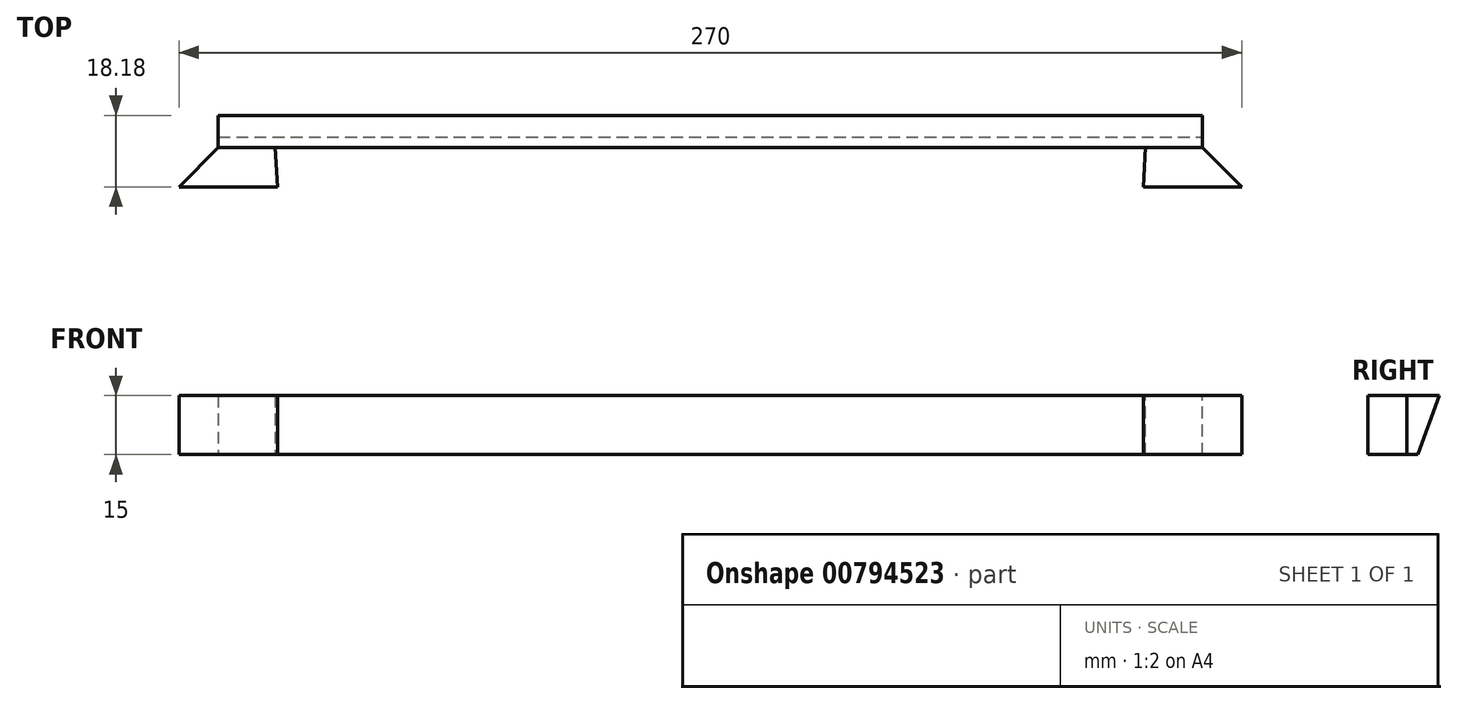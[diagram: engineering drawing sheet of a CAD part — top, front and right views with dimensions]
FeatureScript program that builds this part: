
annotation { "Feature Type Name" : "Feature", "Feature Type Description" : "" }
export const myFeature = defineFeature(function(context is Context, id is Id, definition is map)
    precondition{}
    {
        {
            var Q0;
            Q0=qCreatedBy(makeId("Front.planeOp"),FACE);
            var sketch = newSketch(context, id + "F0", { "sketchPlane" : qUnion([Q0])});
            skLineSegment(sketch, "E0.bottom", {"start": v(135, 7.5) * mm, "end": v(-135, 7.5) * mm});
            skLineSegment(sketch, "E0.top", {"start": v(135, -7.5) * mm, "end": v(-135, -7.5) * mm});
            skLineSegment(sketch, "E0.left", {"start": v(135, 7.5) * mm, "end": v(135, -7.5) * mm});
            skLineSegment(sketch, "E0.right", {"start": v(-135, 7.5) * mm, "end": v(-135, -7.5) * mm});
            skPoint(sketch, "E0.middle", {"position": v(0, 0) * mm});
            skSolve(sketch);
        }
        {
            var Q0;
            Q0 = qSketchRegion(id + "F0", true);
            extrude(context, id + "F1", {"entities" : qUnion([Q0]), "depth" : 10 * mm, "offsetDistance" : 25 * mm});
        }
        {
            var Q0;
            Q0=makeQuery(id+"F1.opExtrude","CAP_EDGE",EDGE,{"disambiguationData":[OSD([sQuery(id+"F0.wireOp",EDGE,"E0.left")])],"isStart":true});
            var Q1;
            Q1=makeQuery(id+"F1.opExtrude","CAP_EDGE",EDGE,{"disambiguationData":[OSD([sQuery(id+"F0.wireOp",EDGE,"E0.right")])],"isStart":true});
            chamfer(context, id + "F2", {"entities" : qUnion([Q0, Q1]), "width" : 10 * mm, "tangentPropagation" : true});
        }
        {
            var Q0;
            Q0=makeQuery(id+"F1.opExtrude","CAP_FACE",FACE,{"disambiguationData":[OSD([sQuery(id+"F0.wireOp",EDGE,"E0.bottom"),sQuery(id+"F0.wireOp",EDGE,"E0.top"),sQuery(id+"F0.wireOp",EDGE,"E0.left"),sQuery(id+"F0.wireOp",EDGE,"E0.right")])],"isStart":true});
            var sketch = newSketch(context, id + "F3", { "sketchPlane" : qUnion([Q0])});
            skSolve(sketch);
        }
        {
            var Q0;
            Q0 = qSketchRegion(id + "F3", true);
            var Q1;
            {var subQ0=sQuery(id+"F0.wireOp",EDGE,"E0.bottom");Q1=makeQuery(id+"F3.imprint","IMPRINT",FACE,{"disambiguationData":[TD([[makeQuery(id+"F3.imprint","IMPRINT",EDGE,{"derivedFrom":makeQuery(id+"F1.opExtrude","CAP_EDGE",EDGE,{"disambiguationData":[OSD([subQ0])],"isStart":true})}),-1.0]])]});}
            extrude(context, id + "F4", {"entities" : qUnion([Q0, Q1]), "depth" : 10 * mm, "offsetDistance" : 25 * mm});
        }
        {
            var Q0;
            Q0=makeQuery(id+"F4.opExtrude","CAP_EDGE",EDGE,{"disambiguationData":[OSD([sQuery(id+"F0.wireOp",EDGE,"E0.top")])],"isStart":false});
            chamfer(context, id + "F5", {"entities" : qUnion([Q0]), "chamferType" : ChamferType.OFFSET_ANGLE, "width" : 20 * mm, "oppositeDirection" : false, "angle" : 20 * degree, "tangentPropagation" : true});
        }
        {
            var Q0;
            Q0=makeQuery(id+"F1.opExtrude","CAP_FACE",FACE,{"disambiguationData":[OSD([sQuery(id+"F0.wireOp",EDGE,"E0.bottom"),sQuery(id+"F0.wireOp",EDGE,"E0.top"),sQuery(id+"F0.wireOp",EDGE,"E0.left"),sQuery(id+"F0.wireOp",EDGE,"E0.right")])],"isStart":false});
            var sketch = newSketch(context, id + "F6", { "sketchPlane" : qUnion([Q0])});
            skLineSegment(sketch, "E1.bottom", {"start": v(-135, 7.5) * mm, "end": v(-110, 7.5) * mm});
            skLineSegment(sketch, "E1.top", {"start": v(-135, -7.5) * mm, "end": v(-110, -7.5) * mm});
            skLineSegment(sketch, "E1.left", {"start": v(-135, 7.5) * mm, "end": v(-135, -7.5) * mm});
            skLineSegment(sketch, "E1.right", {"start": v(-110, 7.5) * mm, "end": v(-110, -7.5) * mm});
            skLineSegment(sketch, "E2.bottom", {"start": v(135, 7.5) * mm, "end": v(110, 7.5) * mm});
            skLineSegment(sketch, "E2.top", {"start": v(135, -7.5) * mm, "end": v(110, -7.5) * mm});
            skLineSegment(sketch, "E2.left", {"start": v(135, 7.5) * mm, "end": v(135, -7.5) * mm});
            skLineSegment(sketch, "E2.right", {"start": v(110, 7.5) * mm, "end": v(110, -7.5) * mm});
            skLineSegment(sketch, "E3.bottom", {"start": v(-110, 7.5) * mm, "end": v(110, 7.5) * mm});
            skLineSegment(sketch, "E3.top", {"start": v(-110, -7.5) * mm, "end": v(110, -7.5) * mm});
            skSolve(sketch);
        }
        {
            var Q0;
            Q0=makeQuery(id+"F6.imprint","IMPRINT",FACE,{"disambiguationData":[TD([[makeQuery(id+"F6.imprint","IMPRINT",EDGE,{"derivedFrom":sQuery(id+"F6.wireOp",EDGE,"E3.bottom")}),1.0]])]});
            extrude(context, id + "F7", {"entities" : qUnion([Q0]), "operationType" : NewBodyOperationType.REMOVE, "oppositeDirection" : true, "depth" : 10 * mm, "offsetDistance" : 25 * mm, "hasDraft" : true, "draftAngle" : 3 * degree});
        }
    });
